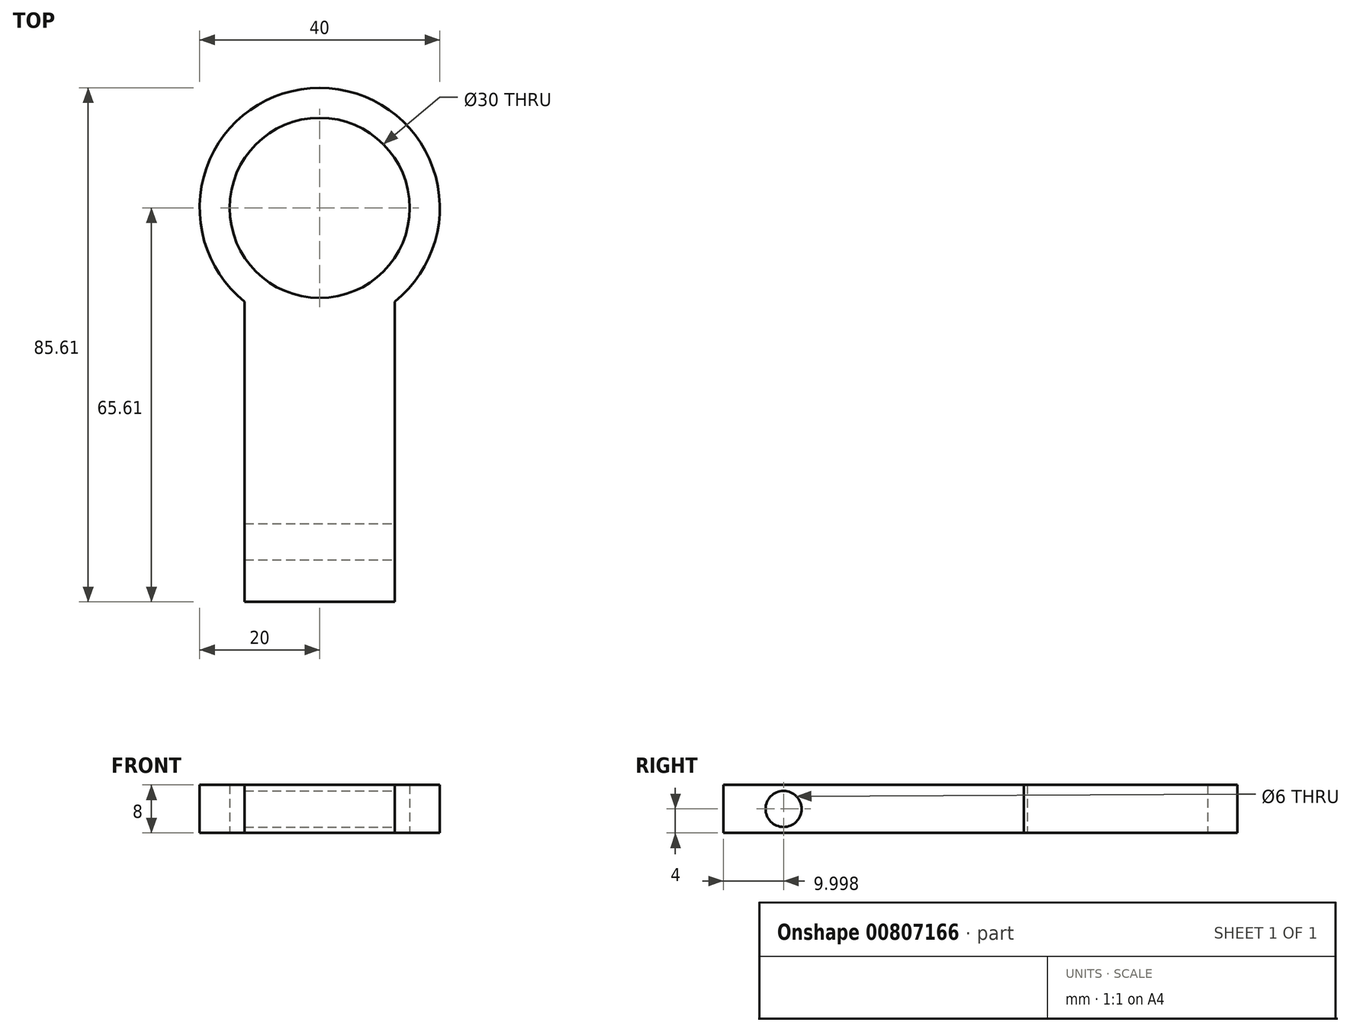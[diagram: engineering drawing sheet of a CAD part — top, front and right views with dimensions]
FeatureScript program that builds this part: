
annotation { "Feature Type Name" : "Feature", "Feature Type Description" : "" }
export const myFeature = defineFeature(function(context is Context, id is Id, definition is map)
    precondition{}
    {
        {
            var Q0;
            Q0=qCreatedBy(makeId("Top.planeOp"),FACE);
            var sketch = newSketch(context, id + "F0", { "sketchPlane" : qUnion([Q0])});
            skCircle(sketch, "E0", {"center": v(0, 0) * mm, "radius": 15 * mm});
            skCircle(sketch, "E1", {"center": v(0, 0) * mm, "radius": 20 * mm});
            skLineSegment(sketch, "E2.bottom", {"start": v(-12.5, -15.61) * mm, "end": v(12.5, -15.61) * mm});
            skLineSegment(sketch, "E2.top", {"start": v(-12.5, -65.61) * mm, "end": v(12.5, -65.61) * mm});
            skLineSegment(sketch, "E2.left", {"start": v(-12.5, -15.61) * mm, "end": v(-12.5, -65.61) * mm});
            skLineSegment(sketch, "E2.right", {"start": v(12.5, -15.61) * mm, "end": v(12.5, -65.61) * mm});
            skSolve(sketch);
        }
        {
            var Q0;
            Q0 = qSketchRegion(id + "F0", true);
            extrude(context, id + "F1", {"entities" : qUnion([Q0]), "depth" : 8 * mm, "offsetDistance" : 25 * mm});
        }
        {
            var Q0;
            Q0=makeQuery(id+"F1.opExtrude","SWEPT_FACE",FACE,{"disambiguationData":[OSD([sQuery(id+"F0.wireOp",EDGE,"E2.right")])]});
            var sketch = newSketch(context, id + "F2", { "sketchPlane" : qUnion([Q0])});
            skPoint(sketch, "E3", {"position": v(-55.61, 4) * mm});
            skPoint(sketch, "E3.positionSnap0", {"position": v(-65.61, 4) * mm});
            skSolve(sketch);
        }
        {
            var Q0;
            Q0=sQuery(id+"F2.wireOp",VERTEX,"E3");
            var Q1;
            Q1=makeQuery(id+"F1.opExtrude","SWEPT_BODY",BODY,{"disambiguationData":[OSD([sQuery(id+"F0.wireOp",EDGE,"E0"),sQuery(id+"F0.wireOp",EDGE,"E1"),sQuery(id+"F0.wireOp",EDGE,"E2.top"),sQuery(id+"F0.wireOp",EDGE,"E2.left"),sQuery(id+"F0.wireOp",EDGE,"E2.right")])]});
            hole(context, id + "F3", {"style" : HoleStyle.SIMPLE, "endStyle" : HoleEndStyle.THROUGH, "holeDiameter" : 6 * mm, "majorDiameter" : 5 * mm, "isTappedThrough" : true, "tappedDepth" : 12 * mm, "tapClearance" : 3, "locations" : qUnion([Q0]), "scope" : qUnion([Q1])});
        }
    });
